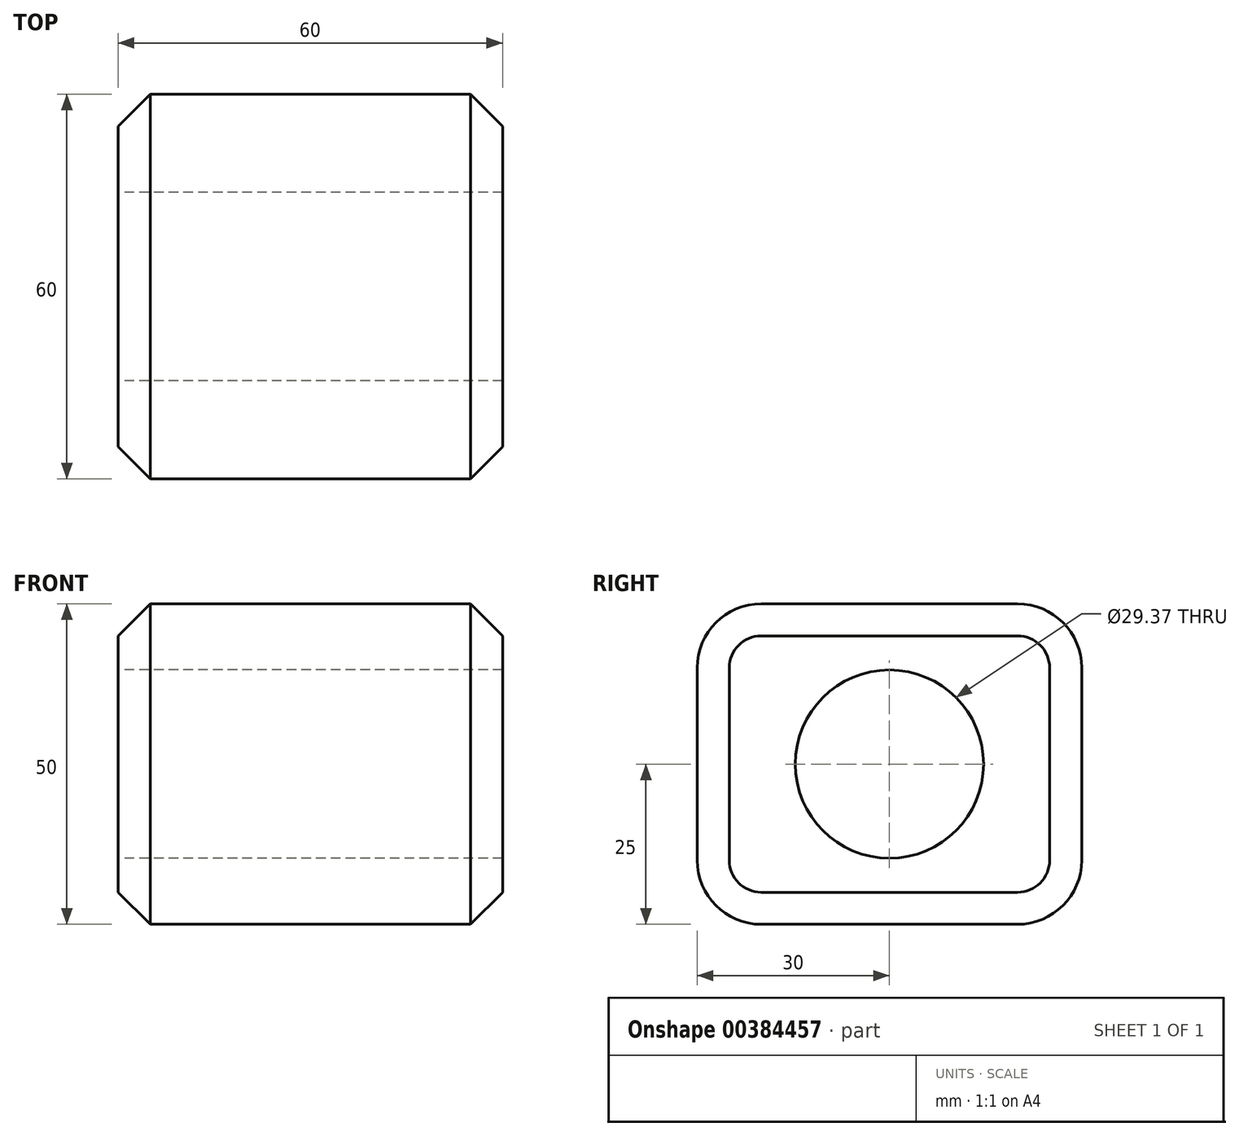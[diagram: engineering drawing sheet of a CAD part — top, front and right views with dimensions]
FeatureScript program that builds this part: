
annotation { "Feature Type Name" : "Feature", "Feature Type Description" : "" }
export const myFeature = defineFeature(function(context is Context, id is Id, definition is map)
    precondition{}
    {
        {
            var Q0;
            Q0=qCreatedBy(makeId("Top.planeOp"),FACE);
            var sketch = newSketch(context, id + "F0", { "sketchPlane" : qUnion([Q0])});
            skLineSegment(sketch, "E0", {"start": v(-30, 30) * mm, "end": v(-30, -30) * mm});
            skLineSegment(sketch, "E1", {"start": v(-30, -30) * mm, "end": v(30, -30) * mm});
            skLineSegment(sketch, "E2", {"start": v(30, -30) * mm, "end": v(30, 30) * mm});
            skLineSegment(sketch, "E3", {"start": v(-30, 30) * mm, "end": v(30, 30) * mm});
            skSolve(sketch);
        }
        {
            var Q0;
            Q0=makeQuery(id+"F0.imprint","IMPRINT",FACE,{"disambiguationData":[TD([[makeQuery(id+"F0.imprint","IMPRINT",EDGE,{"derivedFrom":sQuery(id+"F0.wireOp",EDGE,"E0")}),1.0]])]});
            extrude(context, id + "F1", {"entities" : qUnion([Q0]), "depth" : 25 * mm, "hasSecondDirection" : true, "secondDirectionOppositeDirection" : true, "secondDirectionDepth" : 25 * mm});
        }
        {
            var Q0;
            Q0=makeQuery(id+"F1.opExtrude","SWEPT_FACE",FACE,{"disambiguationData":[OSD([sQuery(id+"F0.wireOp",EDGE,"E0")])]});
            cPlane(context, id + "F2", {"entities" : qUnion([Q0]), "cplaneType" : CPlaneType.OFFSET, "offset" : 0 * mm, "width" : 150 * mm, "height" : 150 * mm});
        }
        {
            var Q0;
            Q0=qCreatedBy(id+"F2.planeOp",FACE);
            var sketch = newSketch(context, id + "F3", { "sketchPlane" : qUnion([Q0])});
            skCircle(sketch, "E4", {"center": v(0, 0) * mm, "radius": 14.69 * mm});
            skSolve(sketch);
        }
        {
            var Q0;
            Q0 = qSketchRegion(id + "F3", true);
            extrude(context, id + "F4", {"entities" : qUnion([Q0]), "operationType" : NewBodyOperationType.REMOVE, "endBound" : BoundingType.THROUGH_ALL, "oppositeDirection" : true, "depth" : 25 * mm});
        }
        {
            var Q0;
            Q0=makeQuery(id+"F1.opExtrude","CAP_EDGE",EDGE,{"disambiguationData":[OSD([sQuery(id+"F0.wireOp",EDGE,"E3")])],"isStart":true});
            var Q1;
            Q1=makeQuery(id+"F1.opExtrude","CAP_EDGE",EDGE,{"disambiguationData":[OSD([sQuery(id+"F0.wireOp",EDGE,"E3")])],"isStart":false});
            var Q2;
            Q2=makeQuery(id+"F1.opExtrude","CAP_EDGE",EDGE,{"disambiguationData":[OSD([sQuery(id+"F0.wireOp",EDGE,"E1")])],"isStart":false});
            var Q3;
            Q3=makeQuery(id+"F1.opExtrude","CAP_EDGE",EDGE,{"disambiguationData":[OSD([sQuery(id+"F0.wireOp",EDGE,"E1")])],"isStart":true});
            fillet(context, id + "F5", {"entities" : qUnion([Q0, Q1, Q2, Q3]), "radius" : 10 * mm, "tangentPropagation" : true, "allowEdgeOverflow" : false});
        }
        {
            var Q0;
            Q0=makeQuery(id+"F1.opExtrude","SWEPT_EDGE",EDGE,{"disambiguationData":[OSD([sQuery(id+"F0.wireOp",EDGE,"E2"),sQuery(id+"F0.wireOp",EDGE,"E3")])]});
            var Q1;
            Q1=makeQuery(id+"F1.opExtrude","SWEPT_EDGE",EDGE,{"disambiguationData":[OSD([sQuery(id+"F0.wireOp",EDGE,"E0"),sQuery(id+"F0.wireOp",EDGE,"E3")])]});
            chamfer(context, id + "F6", {"entities" : qUnion([Q0, Q1]), "chamferType" : ChamferType.OFFSET_ANGLE, "width" : 5 * mm, "oppositeDirection" : false, "angle" : 45 * degree, "tangentPropagation" : true});
        }
    });
